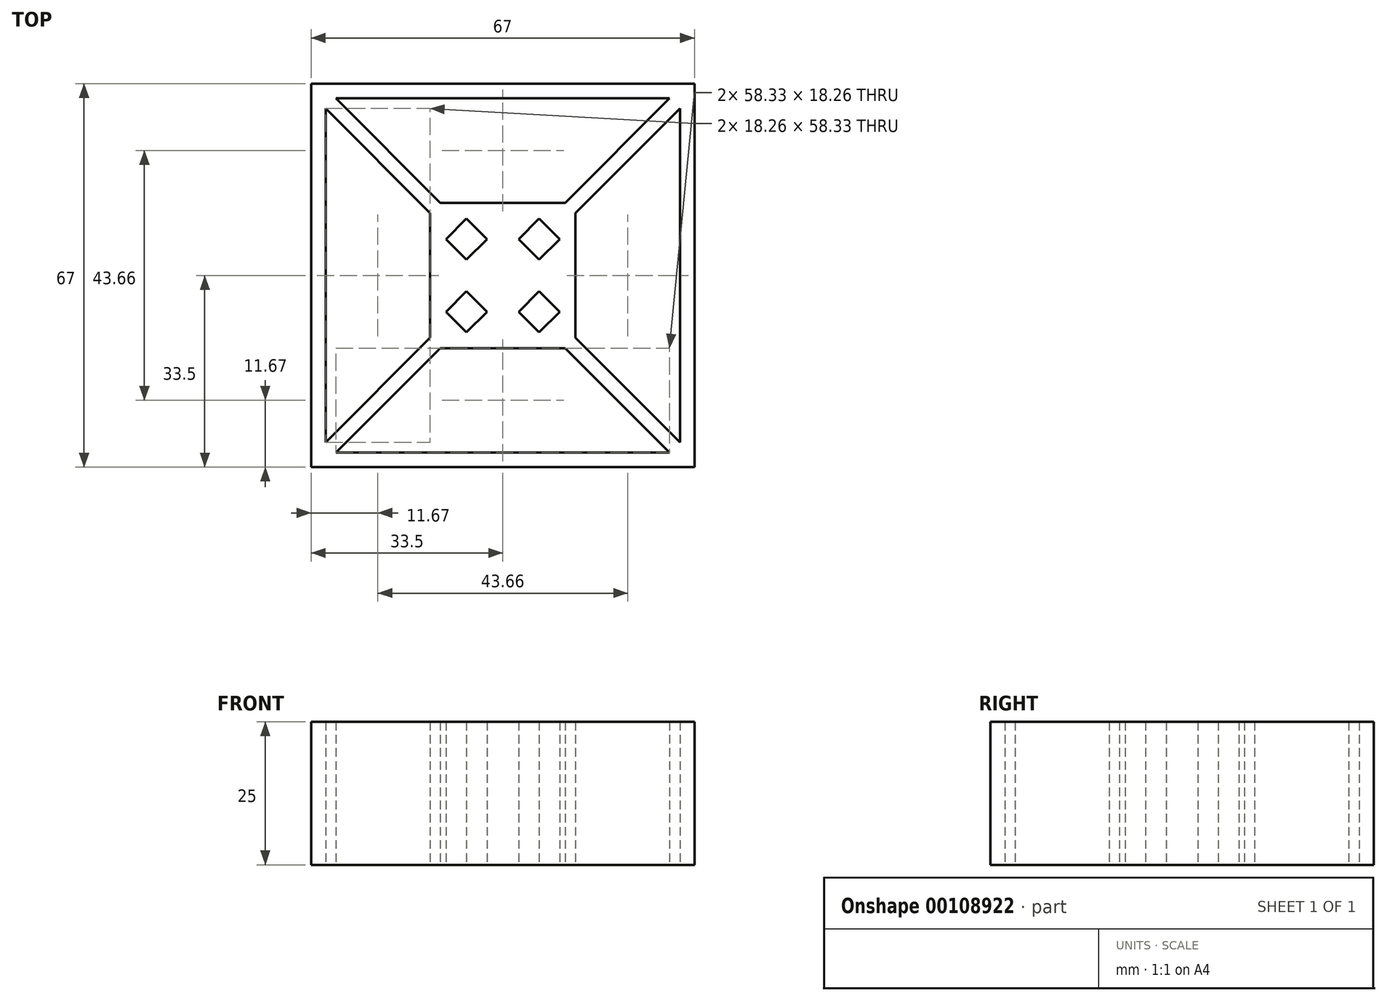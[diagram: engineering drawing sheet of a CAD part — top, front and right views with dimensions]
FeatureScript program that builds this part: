
annotation { "Feature Type Name" : "Feature", "Feature Type Description" : "" }
export const myFeature = defineFeature(function(context is Context, id is Id, definition is map)
    precondition{}
    {
        {
            var Q0;
            Q0=qCreatedBy(makeId("Top.planeOp"),FACE);
            var sketch = newSketch(context, id + "F0", { "sketchPlane" : qUnion([Q0])});
            skLineSegment(sketch, "E0.bottom", {"start": v(0, 0) * mm, "end": v(12.7, 0) * mm, "construction": true});
            skLineSegment(sketch, "E0.top", {"start": v(0, 12.7) * mm, "end": v(10.9, 12.7) * mm});
            skLineSegment(sketch, "E0.left", {"start": v(0, 0) * mm, "end": v(0, 12.7) * mm, "construction": true});
            skLineSegment(sketch, "E0.right", {"start": v(12.7, 0) * mm, "end": v(12.7, 10.9) * mm});
            skLineSegment(sketch, "E1", {"start": v(0, 0) * mm, "end": v(78.23, 78.23) * mm, "construction": true});
            skLineSegment(sketch, "E2", {"start": v(12.7, 10.9) * mm, "end": v(30.96, 29.16) * mm});
            skLineSegment(sketch, "E3.MirrorCS", {"start": v(10.9, 12.7) * mm, "end": v(29.16, 30.96) * mm});
            skLineSegment(sketch, "E4", {"start": v(10.9, 12.7) * mm, "end": v(12.7, 12.7) * mm, "construction": true});
            skLineSegment(sketch, "E5", {"start": v(12.7, 12.7) * mm, "end": v(12.7, 10.9) * mm, "construction": true});
            skLineSegment(sketch, "E6", {"start": v(30.96, 29.16) * mm, "end": v(30.96, 0) * mm});
            skLineSegment(sketch, "E7", {"start": v(33.5, 0) * mm, "end": v(33.5, 33.5) * mm});
            skLineSegment(sketch, "E8.MirrorCS", {"start": v(0, 30.96) * mm, "end": v(0, 33.5) * mm});
            skLineSegment(sketch, "E9.MirrorCS", {"start": v(29.16, 30.96) * mm, "end": v(0, 30.96) * mm});
            skLineSegment(sketch, "E10.MirrorCS", {"start": v(0, 33.5) * mm, "end": v(33.5, 33.5) * mm});
            skPoint(sketch, "E11.middle", {"position": v(6.35, 6.35) * mm});
            skLineSegment(sketch, "E12", {"start": v(6.35, 6.35) * mm, "end": v(13.58, -0.88) * mm, "construction": true});
            skLineSegment(sketch, "E13", {"start": v(6.35, 9.94) * mm, "end": v(9.94, 6.35) * mm});
            skLineSegment(sketch, "E14", {"start": v(9.94, 6.35) * mm, "end": v(6.35, 2.76) * mm});
            skLineSegment(sketch, "E15", {"start": v(6.35, 2.76) * mm, "end": v(2.76, 6.35) * mm});
            skLineSegment(sketch, "E16", {"start": v(2.76, 6.35) * mm, "end": v(6.35, 9.94) * mm});
            skLineSegment(sketch, "E17.MirrorCS", {"start": v(-12.7, 12.7) * mm, "end": v(-12.7, 10.9) * mm, "construction": true});
            skLineSegment(sketch, "E18.MirrorCS", {"start": v(-10.9, 12.7) * mm, "end": v(-12.7, 12.7) * mm, "construction": true});
            skLineSegment(sketch, "E19.MirrorCS", {"start": v(-30.96, 0) * mm, "end": v(-33.5, 0) * mm});
            skLineSegment(sketch, "E20.MirrorCS", {"start": v(-9.94, 6.35) * mm, "end": v(-6.35, 2.76) * mm});
            skLineSegment(sketch, "E21.MirrorCS", {"start": v(-6.35, 9.94) * mm, "end": v(-9.94, 6.35) * mm});
            skLineSegment(sketch, "E22.MirrorCS", {"start": v(-2.76, 6.35) * mm, "end": v(-6.35, 9.94) * mm});
            skLineSegment(sketch, "E23.MirrorCS", {"start": v(-6.35, 2.76) * mm, "end": v(-2.76, 6.35) * mm});
            skLineSegment(sketch, "E24.MirrorCS", {"start": v(-6.35, 6.35) * mm, "end": v(-13.58, -0.88) * mm, "construction": true});
            skLineSegment(sketch, "E25.MirrorCS", {"start": v(-33.5, 0) * mm, "end": v(-33.5, 33.5) * mm});
            skLineSegment(sketch, "E26.MirrorCS", {"start": v(-30.96, 29.16) * mm, "end": v(-30.96, 0) * mm});
            skLineSegment(sketch, "E27.MirrorCS", {"start": v(0, 0) * mm, "end": v(-12.7, 0) * mm, "construction": true});
            skLineSegment(sketch, "E28.MirrorCS", {"start": v(0, 33.5) * mm, "end": v(-33.5, 33.5) * mm});
            skLineSegment(sketch, "E29.MirrorCS", {"start": v(-12.7, 0) * mm, "end": v(-12.7, 10.9) * mm});
            skLineSegment(sketch, "E30.MirrorCS", {"start": v(0, 12.7) * mm, "end": v(-10.9, 12.7) * mm});
            skLineSegment(sketch, "E31.MirrorCS", {"start": v(-12.7, 10.9) * mm, "end": v(-30.96, 29.16) * mm});
            skPoint(sketch, "E32.MirrorP", {"position": v(-6.35, 6.35) * mm});
            skLineSegment(sketch, "E33.MirrorCS", {"start": v(-29.16, 30.96) * mm, "end": v(0, 30.96) * mm});
            skLineSegment(sketch, "E34.MirrorCS", {"start": v(-10.9, 12.7) * mm, "end": v(-29.16, 30.96) * mm});
            skLineSegment(sketch, "E35.MirrorCS", {"start": v(-12.7, -12.7) * mm, "end": v(-12.7, -10.9) * mm, "construction": true});
            skLineSegment(sketch, "E36.MirrorCS", {"start": v(12.7, -12.7) * mm, "end": v(12.7, -10.9) * mm, "construction": true});
            skLineSegment(sketch, "E37.MirrorCS", {"start": v(-10.9, -12.7) * mm, "end": v(-12.7, -12.7) * mm, "construction": true});
            skLineSegment(sketch, "E38.MirrorCS", {"start": v(10.9, -12.7) * mm, "end": v(12.7, -12.7) * mm, "construction": true});
            skLineSegment(sketch, "E39.MirrorCS", {"start": v(6.35, -9.94) * mm, "end": v(9.94, -6.35) * mm});
            skLineSegment(sketch, "E40.MirrorCS", {"start": v(6.35, -2.76) * mm, "end": v(2.76, -6.35) * mm});
            skLineSegment(sketch, "E41.MirrorCS", {"start": v(0, -30.96) * mm, "end": v(0, -33.5) * mm});
            skLineSegment(sketch, "E42.MirrorCS", {"start": v(-6.35, -6.35) * mm, "end": v(-13.58, 0.88) * mm, "construction": true});
            skLineSegment(sketch, "E43.MirrorCS", {"start": v(-2.76, -6.35) * mm, "end": v(-6.35, -9.94) * mm});
            skLineSegment(sketch, "E44.MirrorCS", {"start": v(-6.35, -9.94) * mm, "end": v(-9.94, -6.35) * mm});
            skLineSegment(sketch, "E45.MirrorCS", {"start": v(0, 0) * mm, "end": v(0, -12.7) * mm, "construction": true});
            skLineSegment(sketch, "E46.MirrorCS", {"start": v(6.35, -6.35) * mm, "end": v(13.58, 0.88) * mm, "construction": true});
            skLineSegment(sketch, "E47.MirrorCS", {"start": v(-6.35, -2.76) * mm, "end": v(-2.76, -6.35) * mm});
            skLineSegment(sketch, "E48.MirrorCS", {"start": v(2.76, -6.35) * mm, "end": v(6.35, -9.94) * mm});
            skLineSegment(sketch, "E49.MirrorCS", {"start": v(9.94, -6.35) * mm, "end": v(6.35, -2.76) * mm});
            skLineSegment(sketch, "E50.MirrorCS", {"start": v(-9.94, -6.35) * mm, "end": v(-6.35, -2.76) * mm});
            skLineSegment(sketch, "E51.MirrorCS", {"start": v(-29.16, -30.96) * mm, "end": v(0, -30.96) * mm});
            skLineSegment(sketch, "E52.MirrorCS", {"start": v(33.5, 0) * mm, "end": v(33.5, -33.5) * mm});
            skLineSegment(sketch, "E53.MirrorCS", {"start": v(30.96, -29.16) * mm, "end": v(30.96, 0) * mm});
            skLineSegment(sketch, "E54.MirrorCS", {"start": v(10.9, -12.7) * mm, "end": v(29.16, -30.96) * mm});
            skLineSegment(sketch, "E55.MirrorCS", {"start": v(12.7, -10.9) * mm, "end": v(30.96, -29.16) * mm});
            skLineSegment(sketch, "E56.MirrorCS", {"start": v(12.7, 0) * mm, "end": v(12.7, -10.9) * mm});
            skPoint(sketch, "E57.MirrorP", {"position": v(-6.35, -6.35) * mm});
            skPoint(sketch, "E58.MirrorP", {"position": v(6.35, -6.35) * mm});
            skLineSegment(sketch, "E59.MirrorCS", {"start": v(-10.9, -12.7) * mm, "end": v(-29.16, -30.96) * mm});
            skLineSegment(sketch, "E60.MirrorCS", {"start": v(-30.96, -29.16) * mm, "end": v(-30.96, 0) * mm});
            skLineSegment(sketch, "E61.MirrorCS", {"start": v(0, -12.7) * mm, "end": v(10.9, -12.7) * mm});
            skLineSegment(sketch, "E62.MirrorCS", {"start": v(-12.7, 0) * mm, "end": v(-12.7, -10.9) * mm});
            skLineSegment(sketch, "E63.MirrorCS", {"start": v(0, -12.7) * mm, "end": v(-10.9, -12.7) * mm});
            skLineSegment(sketch, "E64.MirrorCS", {"start": v(0, -33.5) * mm, "end": v(33.5, -33.5) * mm});
            skLineSegment(sketch, "E65.MirrorCS", {"start": v(-33.5, 0) * mm, "end": v(-33.5, -33.5) * mm});
            skLineSegment(sketch, "E66.MirrorCS", {"start": v(0, -33.5) * mm, "end": v(-33.5, -33.5) * mm});
            skLineSegment(sketch, "E67.MirrorCS", {"start": v(29.16, -30.96) * mm, "end": v(0, -30.96) * mm});
            skLineSegment(sketch, "E68.MirrorCS", {"start": v(-12.7, -10.9) * mm, "end": v(-30.96, -29.16) * mm});
            skSolve(sketch);
        }
        {
            var Q0;
            Q0 = qSketchRegion(id + "F0", true);
            extrude(context, id + "F1", {"entities" : qUnion([Q0]), "depth" : 25 * mm});
        }
    });
